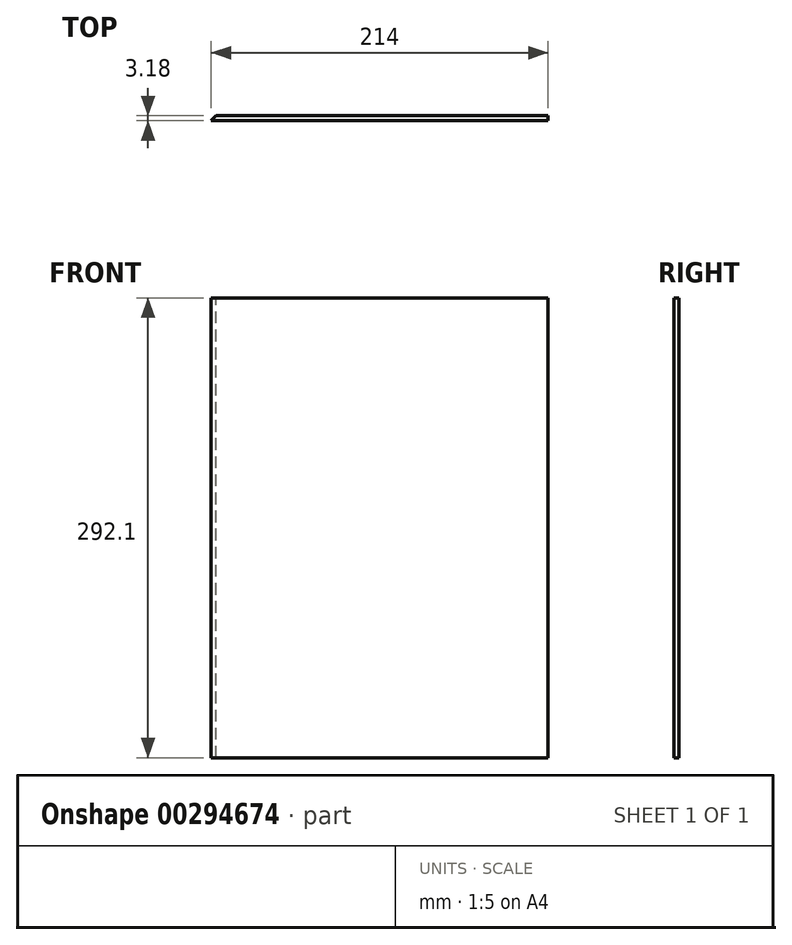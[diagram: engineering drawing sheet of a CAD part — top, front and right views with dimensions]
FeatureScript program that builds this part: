
annotation { "Feature Type Name" : "Feature", "Feature Type Description" : "" }
export const myFeature = defineFeature(function(context is Context, id is Id, definition is map)
    precondition{}
    {
        {
            var Q0;
            Q0=qCreatedBy(makeId("Front.planeOp"),FACE);
            var sketch = newSketch(context, id + "F0", { "sketchPlane" : qUnion([Q0])});
            skLineSegment(sketch, "E0.bottom", {"start": v(-107.95, 146.05) * mm, "end": v(107.95, 146.05) * mm});
            skLineSegment(sketch, "E0.top", {"start": v(-107.95, -146.05) * mm, "end": v(107.95, -146.05) * mm});
            skLineSegment(sketch, "E0.left", {"start": v(-107.95, 146.05) * mm, "end": v(-107.95, -146.05) * mm});
            skLineSegment(sketch, "E0.right", {"start": v(107.95, 146.05) * mm, "end": v(107.95, -146.05) * mm});
            skPoint(sketch, "E0.middle", {"position": v(0, 0) * mm});
            skSolve(sketch);
        }
        {
            var Q0;
            Q0 = qSketchRegion(id + "F0", true);
            extrude(context, id + "F1", {"entities" : qUnion([Q0]), "endBound" : BoundingType.SYMMETRIC, "depth" : 3.17 * mm});
        }
        {
            var Q0;
            Q0=makeQuery(id+"F1.opExtrude","CAP_EDGE",EDGE,{"disambiguationData":[OSD([sQuery(id+"F0.wireOp",EDGE,"E0.left")])],"isStart":true});
            chamfer(context, id + "F2", {"entities" : qUnion([Q0]), "width" : 5.08 * mm, "tangentPropagation" : true});
        }
    });
